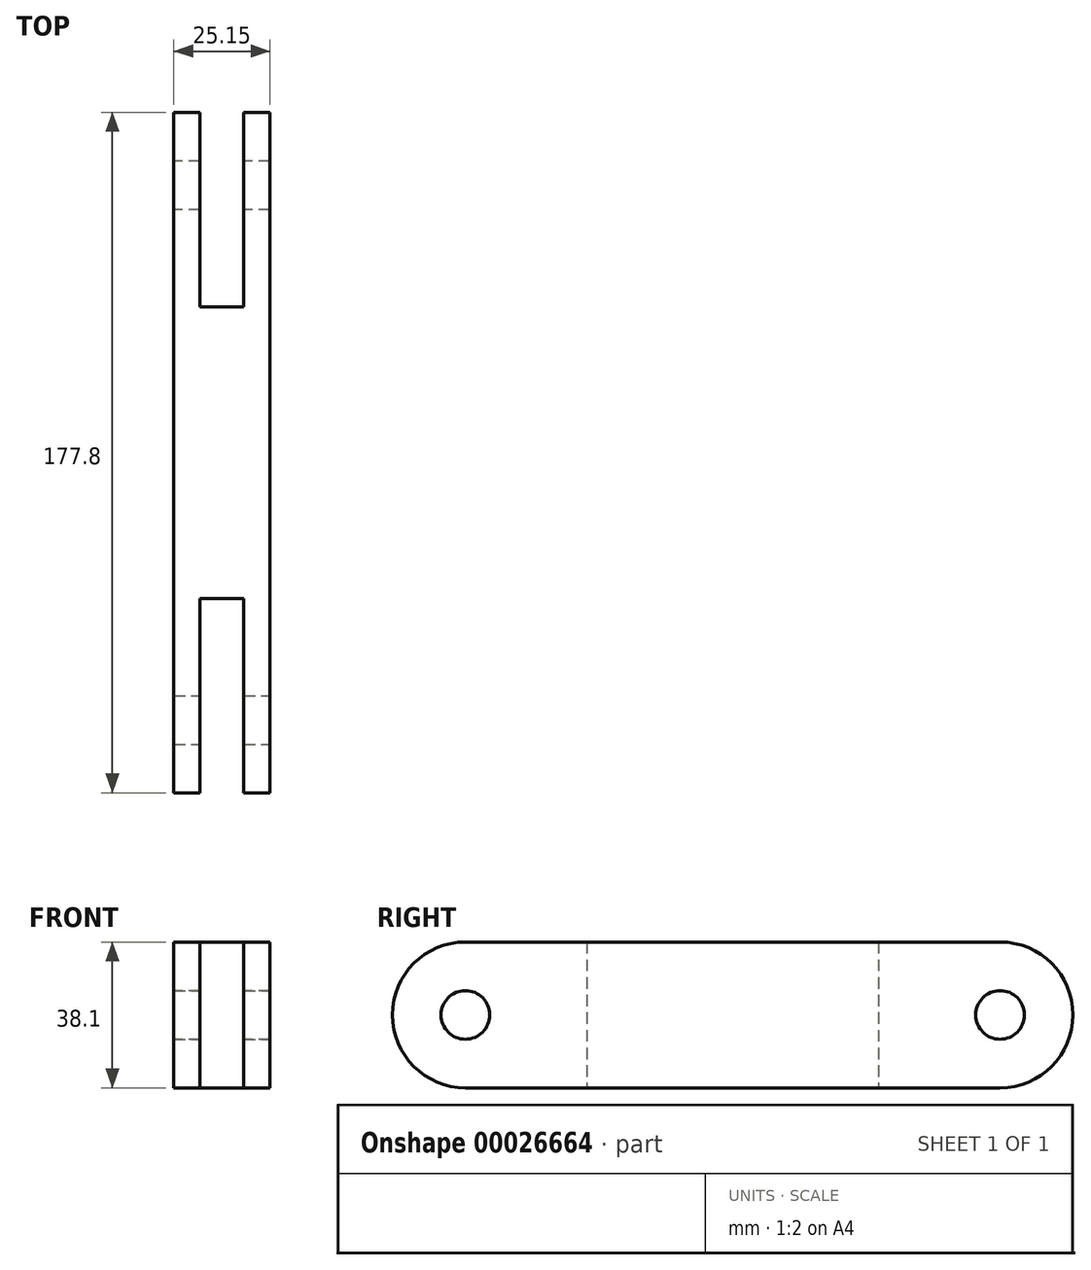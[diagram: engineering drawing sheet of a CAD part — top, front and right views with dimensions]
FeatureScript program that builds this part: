
annotation { "Feature Type Name" : "Feature", "Feature Type Description" : "" }
export const myFeature = defineFeature(function(context is Context, id is Id, definition is map)
    precondition{}
    {
        {
            var Q0;
            Q0=qCreatedBy(makeId("Front.planeOp"),FACE);
            var sketch = newSketch(context, id + "F0", { "sketchPlane" : qUnion([Q0])});
            skLineSegment(sketch, "E0", {"start": v(-21.38, 29.46) * mm, "end": v(-21.38, -8.64) * mm});
            skLineSegment(sketch, "E1", {"start": v(-22.68, -8.64) * mm, "end": v(3.77, -8.64) * mm});
            skLineSegment(sketch, "E2", {"start": v(3.77, -8.64) * mm, "end": v(3.77, 29.46) * mm});
            skLineSegment(sketch, "E3", {"start": v(3.77, 29.46) * mm, "end": v(-21.38, 29.46) * mm});
            skLineSegment(sketch, "E4", {"start": v(-14.52, 29.46) * mm, "end": v(-14.52, -8.64) * mm});
            skLineSegment(sketch, "E5", {"start": v(-3.09, 29.46) * mm, "end": v(-3.09, -8.64) * mm});
            skLineSegment(sketch, "E6", {"start": v(-14.52, 10.41) * mm, "end": v(-21.38, 10.41) * mm});
            skLineSegment(sketch, "E7", {"start": v(-3.09, 10.41) * mm, "end": v(3.77, 10.41) * mm});
            skLineSegment(sketch, "E8", {"start": v(-3.09, 4.2) * mm, "end": v(-14.52, 4.2) * mm});
            skSolve(sketch);
        }
        {
            var Q0;
            {var subQ1=sQuery(id+"F0.wireOp",EDGE,"E8");Q0=makeQuery(id+"F0.imprint","IMPRINT",FACE,{"disambiguationData":[TD([[makeQuery(id+"F0.imprint","IMPRINT",EDGE,{"derivedFrom":subQ1}),-1.0]])]});}
            var Q1;
            {var subQ1=sQuery(id+"F0.wireOp",EDGE,"E6");Q1=makeQuery(id+"F0.imprint","IMPRINT",FACE,{"disambiguationData":[TD([[makeQuery(id+"F0.imprint","IMPRINT",EDGE,{"derivedFrom":subQ1}),-1.0]])]});}
            var Q2;
            {var subQ0=sQuery(id+"F0.wireOp",EDGE,"E7");Q2=makeQuery(id+"F0.imprint","IMPRINT",FACE,{"disambiguationData":[TD([[makeQuery(id+"F0.imprint","IMPRINT",EDGE,{"derivedFrom":subQ0}),1.0]])]});}
            var Q3;
            {var subQ0=sQuery(id+"F0.wireOp",EDGE,"E7");Q3=makeQuery(id+"F0.imprint","IMPRINT",FACE,{"disambiguationData":[TD([[makeQuery(id+"F0.imprint","IMPRINT",EDGE,{"derivedFrom":subQ0}),-1.0]])]});}
            var Q4;
            {var subQ0=sQuery(id+"F0.wireOp",EDGE,"E8");Q4=makeQuery(id+"F0.imprint","IMPRINT",FACE,{"disambiguationData":[TD([[makeQuery(id+"F0.imprint","IMPRINT",EDGE,{"derivedFrom":subQ0}),1.0]])]});}
            var Q5;
            {var subQ0=sQuery(id+"F0.wireOp",EDGE,"E6");Q5=makeQuery(id+"F0.imprint","IMPRINT",FACE,{"disambiguationData":[TD([[makeQuery(id+"F0.imprint","IMPRINT",EDGE,{"derivedFrom":subQ0}),1.0]])]});}
            extrude(context, id + "F1", {"entities" : qUnion([Q0, Q1, Q2, Q3, Q4, Q5]), "oppositeDirection" : true, "depth" : 76.2 * mm});
        }
        {
            var Q0;
            {var subQ1=sQuery(id+"F0.wireOp",EDGE,"E6");Q0=makeQuery(id+"F0.imprint","IMPRINT",FACE,{"disambiguationData":[TD([[makeQuery(id+"F0.imprint","IMPRINT",EDGE,{"derivedFrom":subQ1}),-1.0]])]});}
            var Q1;
            {var subQ0=sQuery(id+"F0.wireOp",EDGE,"E6");Q1=makeQuery(id+"F0.imprint","IMPRINT",FACE,{"disambiguationData":[TD([[makeQuery(id+"F0.imprint","IMPRINT",EDGE,{"derivedFrom":subQ0}),1.0]])]});}
            var Q2;
            {var subQ0=sQuery(id+"F0.wireOp",EDGE,"E7");Q2=makeQuery(id+"F0.imprint","IMPRINT",FACE,{"disambiguationData":[TD([[makeQuery(id+"F0.imprint","IMPRINT",EDGE,{"derivedFrom":subQ0}),1.0]])]});}
            var Q3;
            {var subQ0=sQuery(id+"F0.wireOp",EDGE,"E7");Q3=makeQuery(id+"F0.imprint","IMPRINT",FACE,{"disambiguationData":[TD([[makeQuery(id+"F0.imprint","IMPRINT",EDGE,{"derivedFrom":subQ0}),-1.0]])]});}
            extrude(context, id + "F2", {"entities" : qUnion([Q0, Q1, Q2, Q3]), "operationType" : NewBodyOperationType.ADD, "depth" : 50.8 * mm});
        }
        {
            var Q0;
            {var subQ0=sQuery(id+"F0.wireOp",EDGE,"E3");Q0=makeQuery(id+"F2.opExtrude","CAP_EDGE",EDGE,{"disambiguationData":[OSD([subQ0]),TDD([makeQuery(id+"F0.imprint","IMPRINT",EDGE,{"disambiguationData":[TD([[makeQuery(id+"F0.imprint","INTERSECT",VERTEX,{"derivedFrom":[sQuery(id+"F0.wireOp",EDGE,"E2"),subQ0]}),-1.0]])],"derivedFrom":subQ0})])],"isStart":false});}
            var Q1;
            {var subQ0=sQuery(id+"F0.wireOp",EDGE,"E3");Q1=makeQuery(id+"F2.opExtrude","CAP_EDGE",EDGE,{"disambiguationData":[OSD([subQ0]),TDD([makeQuery(id+"F0.imprint","IMPRINT",EDGE,{"disambiguationData":[TD([[makeQuery(id+"F0.imprint","INTERSECT",VERTEX,{"derivedFrom":[sQuery(id+"F0.wireOp",EDGE,"E0"),subQ0]}),1.0]])],"derivedFrom":subQ0})])],"isStart":false});}
            var Q2;
            {var subQ0=sQuery(id+"F0.wireOp",EDGE,"E1");Q2=makeQuery(id+"F2.opExtrude","CAP_EDGE",EDGE,{"disambiguationData":[OSD([subQ0]),TDD([makeQuery(id+"F0.imprint","IMPRINT",EDGE,{"disambiguationData":[TD([[makeQuery(id+"F0.imprint","INTERSECT",VERTEX,{"derivedFrom":[sQuery(id+"F0.wireOp",EDGE,"E0"),subQ0]}),-1.0]])],"derivedFrom":subQ0})])],"isStart":false});}
            var Q3;
            {var subQ0=sQuery(id+"F0.wireOp",EDGE,"E1");Q3=makeQuery(id+"F2.opExtrude","CAP_EDGE",EDGE,{"disambiguationData":[OSD([subQ0]),TDD([makeQuery(id+"F0.imprint","IMPRINT",EDGE,{"disambiguationData":[TD([[makeQuery(id+"F0.imprint","INTERSECT",VERTEX,{"derivedFrom":[subQ0,sQuery(id+"F0.wireOp",EDGE,"E2")]}),1.0]])],"derivedFrom":subQ0})])],"isStart":false});}
            fillet(context, id + "F3", {"entities" : qUnion([Q0, Q1, Q2, Q3]), "radius" : 19.05 * mm, "tangentPropagation" : true, "allowEdgeOverflow" : false});
        }
        {
            var Q0;
            {var subQ0=sQuery(id+"F0.wireOp",EDGE,"E2");Q0=makeQuery(id+"F2.boolean.opBoolean","MERGE",FACE,{"derivedFrom":[makeQuery(id+"F1.opExtrude","SWEPT_FACE",FACE,{"disambiguationData":[OSD([subQ0])]}),makeQuery(id+"F2.opExtrude","SWEPT_FACE",FACE,{"disambiguationData":[OSD([subQ0])]})]});}
            var sketch = newSketch(context, id + "F4", { "sketchPlane" : qUnion([Q0])});
            skCircle(sketch, "E9", {"center": v(-31.75, 10.41) * mm, "radius": 6.35 * mm});
            skSolve(sketch);
        }
        {
            var Q0;
            Q0=makeQuery(id+"F4.imprint","IMPRINT",FACE,{"disambiguationData":[TD([[makeQuery(id+"F4.imprint","IMPRINT",EDGE,{"derivedFrom":sQuery(id+"F4.wireOp",EDGE,"E9")}),1.0]])]});
            extrude(context, id + "F5", {"entities" : qUnion([Q0]), "operationType" : NewBodyOperationType.REMOVE, "endBound" : BoundingType.THROUGH_ALL, "oppositeDirection" : true, "depth" : 25.4 * mm});
        }
        {
            var Q0;
            Q0=makeQuery(id+"F1.opExtrude","CAP_FACE",FACE,{"disambiguationData":[OSD([sQuery(id+"F0.wireOp",EDGE,"E0"),sQuery(id+"F0.wireOp",EDGE,"E1"),sQuery(id+"F0.wireOp",EDGE,"E2"),sQuery(id+"F0.wireOp",EDGE,"E3")])],"isStart":false});
            var sketch = newSketch(context, id + "F6", { "sketchPlane" : qUnion([Q0])});
            skLineSegment(sketch, "E10", {"start": v(3.09, 29.46) * mm, "end": v(3.09, -8.64) * mm});
            skLineSegment(sketch, "E11", {"start": v(14.52, 29.46) * mm, "end": v(14.52, -8.64) * mm});
            skLineSegment(sketch, "E12", {"start": v(21.38, 10.41) * mm, "end": v(14.52, 10.41) * mm});
            skLineSegment(sketch, "E13", {"start": v(14.52, 4.2) * mm, "end": v(3.09, 4.2) * mm});
            skLineSegment(sketch, "E14", {"start": v(3.09, 10.41) * mm, "end": v(-3.77, 10.41) * mm});
            skSolve(sketch);
        }
        {
            var Q0;
            {var subQ5=sQuery(id+"F6.wireOp",EDGE,"E14");Q0=makeQuery(id+"F6.imprint","IMPRINT",FACE,{"disambiguationData":[TD([[makeQuery(id+"F6.imprint","IMPRINT",EDGE,{"derivedFrom":subQ5}),-1.0]])]});}
            var Q1;
            {var subQ1=sQuery(id+"F6.wireOp",EDGE,"E14");Q1=makeQuery(id+"F6.imprint","IMPRINT",FACE,{"disambiguationData":[TD([[makeQuery(id+"F6.imprint","IMPRINT",EDGE,{"derivedFrom":subQ1}),1.0]])]});}
            var Q2;
            {var subQ5=sQuery(id+"F6.wireOp",EDGE,"E12");Q2=makeQuery(id+"F6.imprint","IMPRINT",FACE,{"disambiguationData":[TD([[makeQuery(id+"F6.imprint","IMPRINT",EDGE,{"derivedFrom":subQ5}),-1.0]])]});}
            var Q3;
            {var subQ1=sQuery(id+"F6.wireOp",EDGE,"E12");Q3=makeQuery(id+"F6.imprint","IMPRINT",FACE,{"disambiguationData":[TD([[makeQuery(id+"F6.imprint","IMPRINT",EDGE,{"derivedFrom":subQ1}),1.0]])]});}
            extrude(context, id + "F7", {"entities" : qUnion([Q0, Q1, Q2, Q3]), "operationType" : NewBodyOperationType.ADD, "depth" : 50.8 * mm});
        }
        {
            var Q0;
            {var subQ0=sQuery(id+"F0.wireOp",EDGE,"E3");var subQ1=makeQuery(id+"F1.opExtrude","CAP_EDGE",EDGE,{"disambiguationData":[OSD([subQ0])],"isStart":false});Q0=makeQuery(id+"F7.opExtrude","CAP_EDGE",EDGE,{"disambiguationData":[OSD([subQ0]),TDD([makeQuery(id+"F6.imprint","IMPRINT",EDGE,{"disambiguationData":[TD([[makeQuery(id+"F6.imprint","INTERSECT",VERTEX,{"derivedFrom":[makeQuery(id+"F1.opExtrude","CAP_EDGE",EDGE,{"disambiguationData":[OSD([sQuery(id+"F0.wireOp",EDGE,"E0")])],"isStart":false}),subQ1]}),1.0]])],"derivedFrom":subQ1})])],"isStart":false});}
            var Q1;
            {var subQ0=sQuery(id+"F0.wireOp",EDGE,"E3");var subQ1=makeQuery(id+"F1.opExtrude","CAP_EDGE",EDGE,{"disambiguationData":[OSD([subQ0])],"isStart":false});Q1=makeQuery(id+"F7.opExtrude","CAP_EDGE",EDGE,{"disambiguationData":[OSD([subQ0]),TDD([makeQuery(id+"F6.imprint","IMPRINT",EDGE,{"disambiguationData":[TD([[makeQuery(id+"F6.imprint","INTERSECT",VERTEX,{"derivedFrom":[makeQuery(id+"F1.opExtrude","CAP_EDGE",EDGE,{"disambiguationData":[OSD([sQuery(id+"F0.wireOp",EDGE,"E2")])],"isStart":false}),subQ1]}),-1.0]])],"derivedFrom":subQ1})])],"isStart":false});}
            var Q2;
            {var subQ0=sQuery(id+"F0.wireOp",EDGE,"E1");var subQ1=makeQuery(id+"F1.opExtrude","CAP_EDGE",EDGE,{"disambiguationData":[OSD([subQ0])],"isStart":false});Q2=makeQuery(id+"F7.opExtrude","CAP_EDGE",EDGE,{"disambiguationData":[OSD([subQ0]),TDD([makeQuery(id+"F6.imprint","IMPRINT",EDGE,{"disambiguationData":[TD([[makeQuery(id+"F6.imprint","INTERSECT",VERTEX,{"derivedFrom":[subQ1,makeQuery(id+"F1.opExtrude","CAP_EDGE",EDGE,{"disambiguationData":[OSD([sQuery(id+"F0.wireOp",EDGE,"E2")])],"isStart":false})]}),1.0]])],"derivedFrom":subQ1})])],"isStart":false});}
            var Q3;
            {var subQ0=sQuery(id+"F0.wireOp",EDGE,"E1");var subQ1=makeQuery(id+"F1.opExtrude","CAP_EDGE",EDGE,{"disambiguationData":[OSD([subQ0])],"isStart":false});Q3=makeQuery(id+"F7.opExtrude","CAP_EDGE",EDGE,{"disambiguationData":[OSD([subQ0]),TDD([makeQuery(id+"F6.imprint","IMPRINT",EDGE,{"disambiguationData":[TD([[makeQuery(id+"F6.imprint","INTERSECT",VERTEX,{"derivedFrom":[makeQuery(id+"F1.opExtrude","CAP_EDGE",EDGE,{"disambiguationData":[OSD([sQuery(id+"F0.wireOp",EDGE,"E0")])],"isStart":false}),subQ1]}),-1.0]])],"derivedFrom":subQ1})])],"isStart":false});}
            fillet(context, id + "F8", {"entities" : qUnion([Q0, Q1, Q2, Q3]), "radius" : 19.05 * mm, "tangentPropagation" : true, "allowEdgeOverflow" : false});
        }
        {
            var Q0;
            {var subQ0=sQuery(id+"F0.wireOp",EDGE,"E0");Q0=makeQuery(id+"F7.boolean.opBoolean","MERGE",FACE,{"derivedFrom":[makeQuery(id+"F2.boolean.opBoolean","MERGE",FACE,{"derivedFrom":[makeQuery(id+"F1.opExtrude","SWEPT_FACE",FACE,{"disambiguationData":[OSD([subQ0])]}),makeQuery(id+"F2.opExtrude","SWEPT_FACE",FACE,{"disambiguationData":[OSD([subQ0])]})]}),makeQuery(id+"F7.opExtrude","SWEPT_FACE",FACE,{"disambiguationData":[OSD([subQ0])]})]});}
            var sketch = newSketch(context, id + "F9", { "sketchPlane" : qUnion([Q0])});
            skCircle(sketch, "E15", {"center": v(-107.95, 10.41) * mm, "radius": 6.35 * mm});
            skSolve(sketch);
        }
        {
            var Q0;
            Q0=makeQuery(id+"F9.imprint","IMPRINT",FACE,{"disambiguationData":[TD([[makeQuery(id+"F9.imprint","IMPRINT",EDGE,{"derivedFrom":sQuery(id+"F9.wireOp",EDGE,"E15")}),1.0]])]});
            extrude(context, id + "F10", {"entities" : qUnion([Q0]), "operationType" : NewBodyOperationType.REMOVE, "endBound" : BoundingType.THROUGH_ALL, "oppositeDirection" : true, "depth" : 25.4 * mm});
        }
    });
